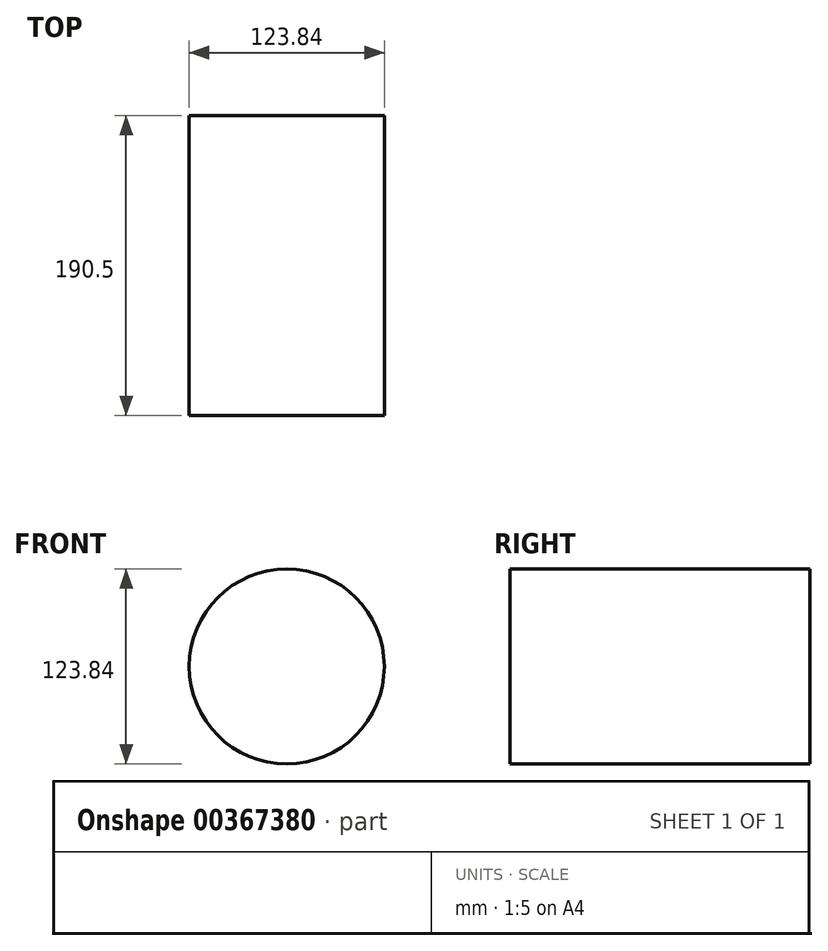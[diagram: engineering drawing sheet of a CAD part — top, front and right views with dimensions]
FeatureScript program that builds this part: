
annotation { "Feature Type Name" : "Feature", "Feature Type Description" : "" }
export const myFeature = defineFeature(function(context is Context, id is Id, definition is map)
    precondition{}
    {
        {
            var Q0;
            Q0=qCreatedBy(makeId("Front.planeOp"),FACE);
            var sketch = newSketch(context, id + "F0", { "sketchPlane" : qUnion([Q0])});
            skCircle(sketch, "E0", {"center": v(2.53, -2.79) * mm, "radius": 61.92 * mm});
            skSolve(sketch);
        }
        {
            var Q0;
            Q0=makeQuery(id+"F0.imprint","IMPRINT",FACE,{"disambiguationData":[TD([[makeQuery(id+"F0.imprint","IMPRINT",EDGE,{"derivedFrom":sQuery(id+"F0.wireOp",EDGE,"E0")}),1.0]])]});
            extrude(context, id + "F1", {"entities" : qUnion([Q0]), "depth" : 190.5 * mm});
        }
    });
